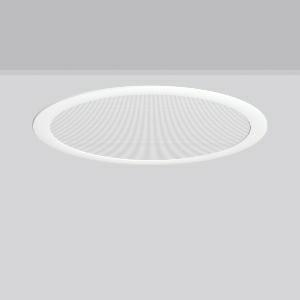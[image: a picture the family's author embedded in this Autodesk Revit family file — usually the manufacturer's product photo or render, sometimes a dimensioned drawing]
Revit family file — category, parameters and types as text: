
# Revit family: toledo_flat_round_e_901586_002_76_fc0c
name_source: partatom
category: Lighting Fixtures
units: mm (PartAtom-declared; Revit-internal decimal feet)

## family parameters
Cut with Voids When Loaded = No
Host = Face
Light Source = No
Part Type = Normal
Room Calculation Point = No
Round Connector Dimension = Use Diameter
Shared = No

## types (1)
- TOLEDO FLAT round E (1 x LED Modul 830, 3450 lm, 3000)
    Apparent Load = 30 VA
    CIE Flux Codes = 62 86 96 100 100
    Color Rendering = 80
    Color Temperature = 3000
    Default Elevation = 1800 mm
    Description = Series: TOLEDO FLAT round
Ultra thin recessed downlight. Housing: die-cast aluminium. Lightguide and diffuser made of non-yellowing PMMA, prismatic. Ceiling installation with spring system. Mounting depth depends on ceiling strength. Including separate LED converter with connecting cable 250 mm. Suitable for through-wiring with separately available accessories. Surface mounted housing as accessory for all sizes. Retrofittable decorative cylinders made of chintz fabric as accessory, optional with satin finish plastic diffuser. Through-wiring box (5 pole) available as accessory. 
Colour: white
Diameter: 495 mm
Height: 6 mm
Cut-out diameter: 470 mm
Recess height: 40-59 mm
Luminaire: recess height: 31-51 mm
Lamp: LED
Socket: without socket
Colour temperature: 3000K
Colour rendering index (CRI): 80
System power: 30 W
Rated luminous flux: 3450 lm
Luminous efficiency: 115 lm/W
Control gear: Converter, dimmable, DALI
Protection class: II
Type of protection: IP 54
    Height = 0 mm  [stored 0 ft]
    Lamp = 1 x LED Modul 830
    Lamp Light Flux = 3450 lm
    Lamp count = 1
    Length = 495 mm
    Lifetime = 50000 h
    Luminous efficacy = 115 lm/W
    Manufacturer = RZB
    ModVariant = No
    Model = 901586.002.76
    Mounting Place = Ceiling
    Mounting Type = Recessed
    Number of Poles = 1
    OnlyDefault = Yes
    Power Factor = 1
    Product Name = TOLEDO FLAT round E
    Product group = Recessed downlights
    ProductGroupID = 402
    Protection Class = Protection class II
    Protection Degree = IP 20
    RLX_Detail_Level = 1
    RLX_Emergency_Light_Flux = 0 lm
    RLX_Emergency_Type = 0
    RLX_Emergency_Type_DB = No
    RlxData = <blob elided: 38285 chars, md5=dcb9b9af>
    Socket = socket
    Standby Power = 0 W
    System Light Flux = 3450 lm
    System Power = 30 W
    Type Comments = Product without accessories
    Type Image = 901586.002.jpg
    URL = http://relux.com
    VarID = ---
    Voltage = 230 V
    Voltage Range = 220-240 V
    Weight = 0.00 kg
    Width = 0 mm  [stored 0 ft]

note: [stored X ft] marks values corroborated as IEEE doubles in the binary element streams (Revit-internal decimal feet)

## geometry (parser evidence)
native form markers: Blend x4, Sweep x8
no freeform markers — native parametric forms only
